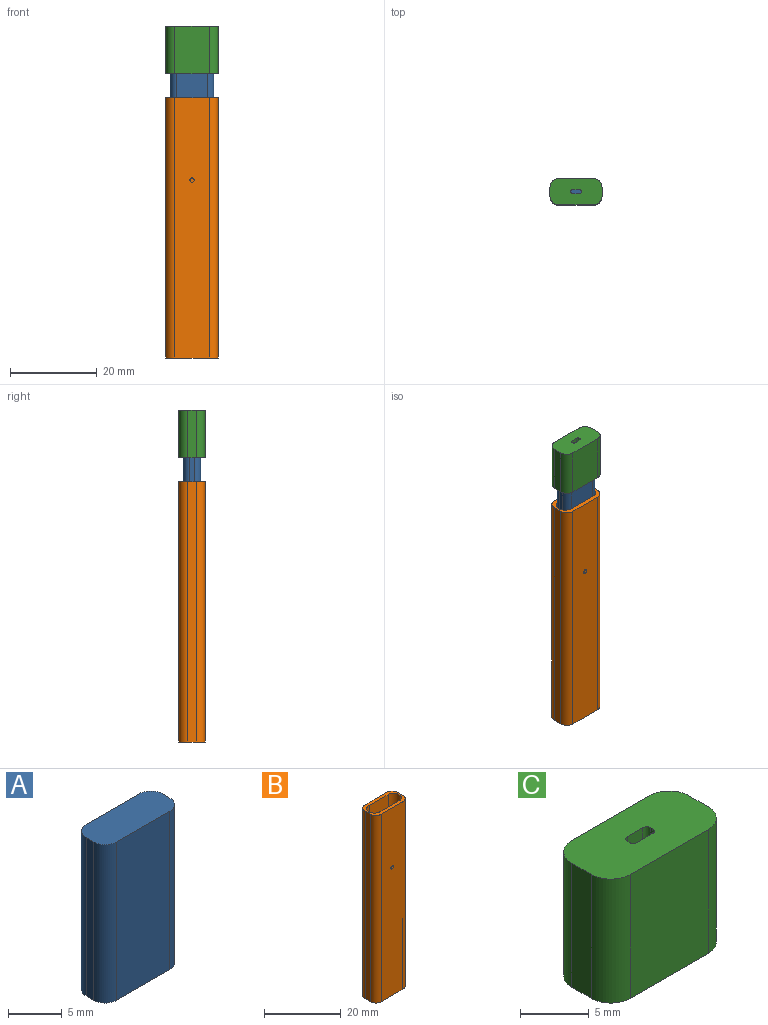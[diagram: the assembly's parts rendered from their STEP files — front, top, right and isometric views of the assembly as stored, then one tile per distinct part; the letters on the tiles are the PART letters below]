
ASSEMBLY  parts=3 mates=1
PART A: 18 faces, bbox 10x4x18 mm
  f0: plane 18x7mm, normal (0,-1,0), area 126mm2, adj f4,f5,f6,f9
  f1: plane 18x1mm, normal (1,0,0), area 18mm2, adj f4,f5,f6,f7
  f2: plane 18x7mm, normal (0,1,0), area 126mm2, adj f4,f5,f7,f8
  f3: plane 18x1mm, normal (-1,0,0), area 18mm2, adj f4,f5,f8,f9
  f4: plane 10x4mm, normal (0,0,1), area 38.1mm2, adj f0,f1,f2,f3,f6,f7,f8,f9
  f5: plane 10x4mm, normal (0,0,-1), area 34.9mm2, adj f0,f1,f2,f3,f6,f7,f8,f9
  f6: cylinder r=1.5mm len=18mm, axis (0,0,1), area 42.4mm2, adj f0,f1,f4,f5
  f7: cylinder r=1.5mm len=18mm, axis (0,0,-1), area 42.4mm2, adj f1,f2,f4,f5
  f8: cylinder r=1.5mm len=18mm, axis (0,0,1), area 42.4mm2, adj f2,f3,f4,f5
  f9: cylinder r=1.5mm len=18mm, axis (0,0,-1), area 42.4mm2, adj f0,f3,f4,f5
  f10: cylinder r=0.5mm len=2mm, axis (0,0,-1), area 6.3mm2, adj f5,f11
  f11: plane 1x1mm, normal (0,0,-1), area 0.8mm2, adj f10
  f12: cylinder r=0.5mm len=2mm, axis (0,0,-1), area 6.3mm2, adj f5,f13
  f13: plane 1x1mm, normal (0,0,-1), area 0.8mm2, adj f12
  f14: cylinder r=0.5mm len=2mm, axis (0,0,-1), area 6.3mm2, adj f5,f15
  f15: plane 1x1mm, normal (0,0,-1), area 0.8mm2, adj f14
  f16: cylinder r=0.5mm len=2mm, axis (0,0,-1), area 6.3mm2, adj f5,f17
  f17: plane 1x1mm, normal (0,0,-1), area 0.8mm2, adj f16
PART B: 26 faces, bbox 12x6x60 mm
  f0: plane 12x6mm, normal (0,0,-1), area 30.5mm2, adj f2,f3,f4,f5,f11,f12,f13,f14
  f1: plane 12x6mm, normal (0,0,1), area 28mm2, adj f2,f3,f4,f5,f6,f7,f9,f10
  f2: plane 60x8mm, normal (0,-1,0), area 479.2mm2, adj f0,f1,f16,f19,f24
  f3: plane 60x2mm, normal (1,0,0), area 120mm2, adj f0,f1,f16,f17
  f4: plane 60x8mm, normal (0,1,0), area 480mm2, adj f0,f1,f17,f18
  f5: plane 60x2mm, normal (-1,0,0), area 120mm2, adj f0,f1,f18,f19
  f6: plane 15.5x7mm, normal (0,1,0), area 108.5mm2, adj f1,f8,f9,f10
  f7: plane 15.5x7mm, normal (0,-1,0), area 108.5mm2, adj f1,f8,f9,f10
  f8: plane 11x4mm, normal (0,0,1), area 40.6mm2, adj f6,f7,f9,f10
  f9: cylinder r=2mm len=15.5mm, axis (0,0,-1), area 97.4mm2, adj f1,f6,f7,f8
  f10: cylinder r=2mm len=15.5mm, axis (0,0,-1), area 97.4mm2, adj f1,f6,f7,f8
  f11: plane 7x5mm, normal (0,-1,0), area 35mm2, adj f0,f15,f20,f23
  f12: plane 5x1mm, normal (-1,0,0), area 5mm2, adj f0,f15,f20,f21
  f13: plane 7x5mm, normal (0,1,0), area 35mm2, adj f0,f15,f21,f22
  f14: plane 5x1mm, normal (1,0,0), area 5mm2, adj f0,f15,f22,f23
  f15: plane 10x4mm, normal (0,0,-1), area 38.1mm2, adj f11,f12,f13,f14,f20,f21,f22,f23
  f16: cylinder r=2mm len=60mm, axis (0,0,1), area 188.5mm2, adj f0,f1,f2,f3
  f17: cylinder r=2mm len=60mm, axis (0,0,-1), area 188.5mm2, adj f0,f1,f3,f4
  f18: cylinder r=2mm len=60mm, axis (0,0,1), area 188.5mm2, adj f0,f1,f4,f5
  f19: cylinder r=2mm len=60mm, axis (0,0,-1), area 188.5mm2, adj f0,f1,f2,f5
  f20: cylinder r=1.5mm len=5mm, axis (0,0,-1), area 11.8mm2, adj f0,f11,f12,f15
  f21: cylinder r=1.5mm len=5mm, axis (0,0,1), area 11.8mm2, adj f0,f12,f13,f15
  f22: cylinder r=1.5mm len=5mm, axis (0,0,-1), area 11.8mm2, adj f0,f13,f14,f15
  f23: cylinder r=1.5mm len=5mm, axis (0,0,1), area 11.8mm2, adj f0,f11,f14,f15
  f24: cylinder r=0.5mm len=1mm, axis (0,-1,0), area 1.6mm2, adj f2,f25
  f25: plane 1x1mm, normal (0,-1,0), area 0.8mm2, adj f24
PART C: 27 faces, bbox 12x6x11 mm
  f0: plane 12x6mm, normal (0,0,1), area 66.3mm2, adj f3,f4,f5,f6,f11,f12,f13,f14
  f1: plane 10x4mm, normal (0,0,-1), area 35.8mm2, adj f7,f8,f9,f10,f15,f16,f17,f18
  f2: plane 12x6mm, normal (0,0,-1), area 30.5mm2, adj f3,f4,f5,f6,f7,f8,f9,f10
  f3: plane 11x8mm, normal (0,-1,0), area 88mm2, adj f0,f2,f11,f14
  f4: plane 11x2mm, normal (1,0,0), area 22mm2, adj f0,f2,f11,f12
  f5: plane 11x8mm, normal (0,1,0), area 88mm2, adj f0,f2,f12,f13
  f6: plane 11x2mm, normal (-1,0,0), area 22mm2, adj f0,f2,f13,f14
  f7: plane 9.5x7mm, normal (0,-1,0), area 66.5mm2, adj f1,f2,f15,f18
  f8: plane 9.5x1mm, normal (-1,0,0), area 9.5mm2, adj f1,f2,f15,f16
  f9: plane 9.5x7mm, normal (0,1,0), area 66.5mm2, adj f1,f2,f16,f17
  f10: plane 9.5x1mm, normal (1,0,0), area 9.5mm2, adj f1,f2,f17,f18
  f11: cylinder r=2mm len=11mm, axis (0,0,1), area 34.6mm2, adj f0,f2,f3,f4
  f12: cylinder r=2mm len=11mm, axis (0,0,-1), area 34.6mm2, adj f0,f2,f4,f5
  f13: cylinder r=2mm len=11mm, axis (0,0,1), area 34.6mm2, adj f0,f2,f5,f6
  f14: cylinder r=2mm len=11mm, axis (0,0,-1), area 34.6mm2, adj f0,f2,f3,f6
  f15: cylinder r=1.5mm len=9.5mm, axis (0,0,-1), area 22.4mm2, adj f1,f2,f7,f8
  f16: cylinder r=1.5mm len=9.5mm, axis (0,0,1), area 22.4mm2, adj f1,f2,f8,f9
  f17: cylinder r=1.5mm len=9.5mm, axis (0,0,-1), area 22.4mm2, adj f1,f2,f9,f10
  f18: cylinder r=1.5mm len=9.5mm, axis (0,0,1), area 22.4mm2, adj f1,f2,f7,f10
  f19: plane 1.6x1.5mm, normal (0,1,0), area 2.4mm2, adj f0,f1,f23,f26
  f20: plane 1.5x0.2mm, normal (-1,0,0), area 0.3mm2, adj f0,f1,f23,f24
  f21: plane 1.6x1.5mm, normal (0,-1,0), area 2.4mm2, adj f0,f1,f24,f25
  f22: plane 1.5x0.2mm, normal (1,0,0), area 0.3mm2, adj f0,f1,f25,f26
  f23: cylinder r=0.4mm len=1.5mm, axis (0,0,1), area 0.9mm2, adj f0,f1,f19,f20
  f24: cylinder r=0.4mm len=1.5mm, axis (0,0,-1), area 0.9mm2, adj f0,f1,f20,f21
  f25: cylinder r=0.4mm len=1.5mm, axis (0,0,1), area 0.9mm2, adj f0,f1,f21,f22
  f26: cylinder r=0.4mm len=1.5mm, axis (0,0,-1), area 0.9mm2, adj f0,f1,f19,f22
PLACE A t=(8.81,21.69,46.93)mm
PLACE B t=(8.8,21.7,-10.08)mm
PLACE C t=(8.81,21.69,55.43)mm
MATE fastened C.f1 <-> A.f4  axis (0,0,-1) through (8.81,21.69,64.93)mm
